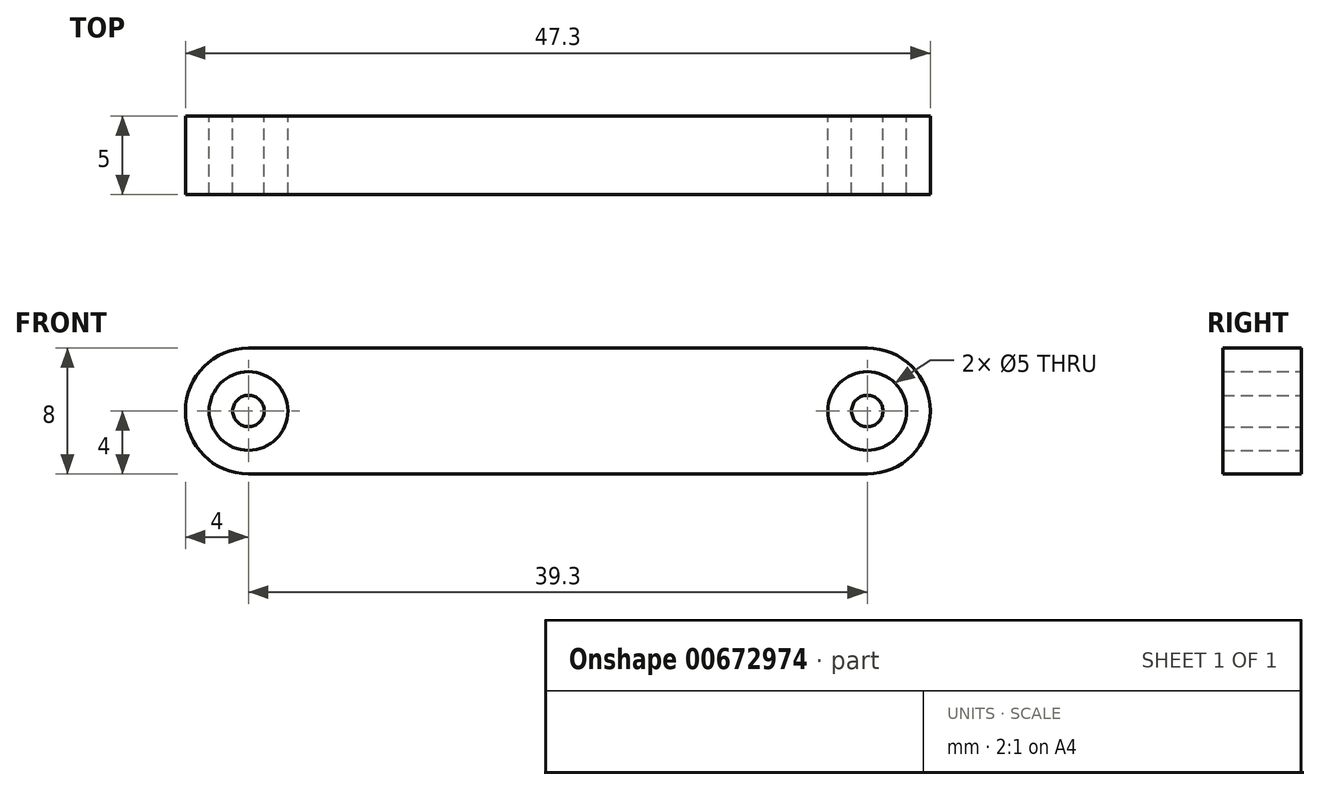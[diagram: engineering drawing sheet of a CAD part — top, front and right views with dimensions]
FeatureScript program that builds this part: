
annotation { "Feature Type Name" : "Feature", "Feature Type Description" : "" }
export const myFeature = defineFeature(function(context is Context, id is Id, definition is map)
    precondition{}
    {
        {
            var Q0;
            Q0=qCreatedBy(makeId("Front.planeOp"),FACE);
            var sketch = newSketch(context, id + "F0", { "sketchPlane" : qUnion([Q0])});
            skArc(sketch, "E0", {"start": v(0, 4) * mm, "mid": v(-4, 0) * mm, "end": v(0, -4) * mm});
            skArc(sketch, "E1", {"start": v(39.3, -4) * mm, "mid": v(43.3, 0) * mm, "end": v(39.3, 4) * mm});
            skCircle(sketch, "E2", {"center": v(0, 0) * mm, "radius": 2.5 * mm});
            skCircle(sketch, "E3", {"center": v(39.3, 0) * mm, "radius": 2.5 * mm});
            skLineSegment(sketch, "E4", {"start": v(0, 4) * mm, "end": v(39.3, 4) * mm});
            skLineSegment(sketch, "E5", {"start": v(39.3, -4) * mm, "end": v(0, -4) * mm});
            skCircle(sketch, "E6", {"center": v(0, 0) * mm, "radius": 1 * mm});
            skCircle(sketch, "E7", {"center": v(39.3, 0) * mm, "radius": 1 * mm});
            skSolve(sketch);
        }
        {
            var Q0;
            Q0 = qSketchRegion(id + "F0", true);
            var Q1;
            Q1=makeQuery(id+"F0.imprint","IMPRINT",FACE,{"disambiguationData":[TD([[makeQuery(id+"F0.imprint","IMPRINT",EDGE,{"derivedFrom":sQuery(id+"F0.wireOp",EDGE,"E6")}),1.0]])]});
            var Q2;
            Q2=makeQuery(id+"F0.imprint","IMPRINT",FACE,{"disambiguationData":[TD([[makeQuery(id+"F0.imprint","IMPRINT",EDGE,{"derivedFrom":sQuery(id+"F0.wireOp",EDGE,"E7")}),1.0]])]});
            extrude(context, id + "F1", {"entities" : qUnion([Q0, Q1, Q2]), "depth" : 5 * mm, "offsetDistance" : 25 * mm});
        }
    });
